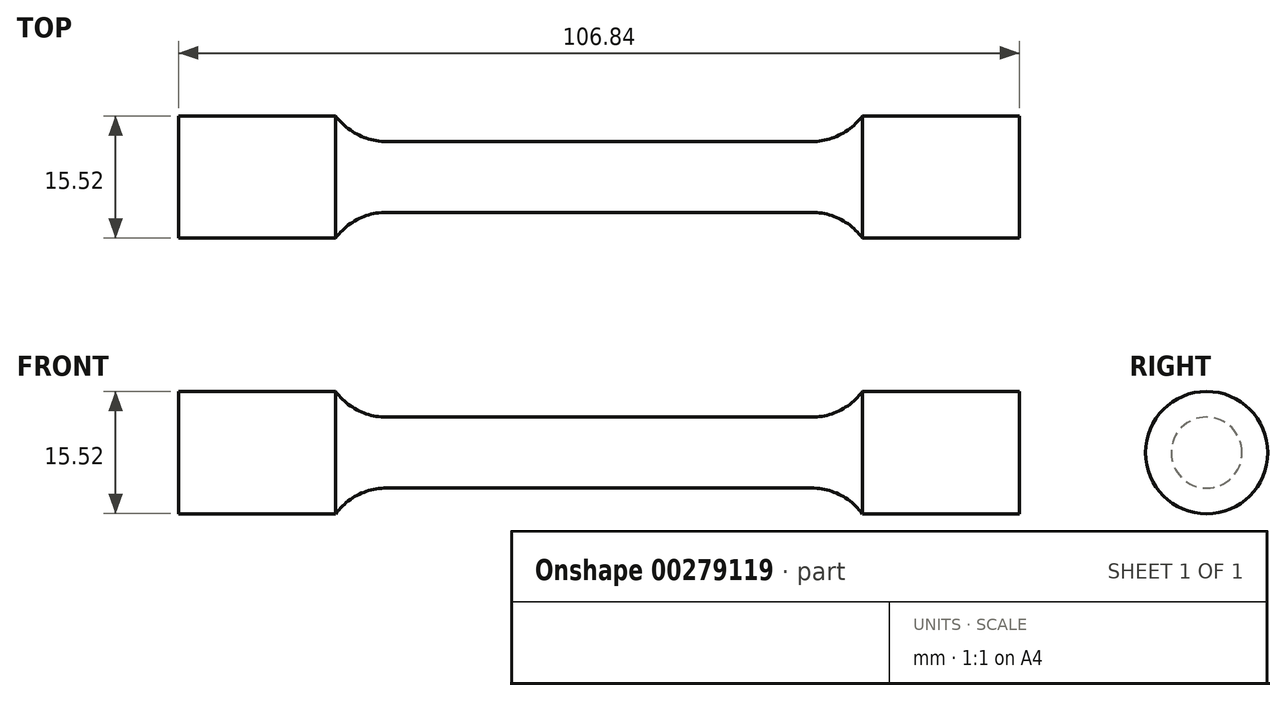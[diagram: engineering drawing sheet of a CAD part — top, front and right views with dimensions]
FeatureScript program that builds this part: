
annotation { "Feature Type Name" : "Feature", "Feature Type Description" : "" }
export const myFeature = defineFeature(function(context is Context, id is Id, definition is map)
    precondition{}
    {
        {
            var Q0;
            Q0=qCreatedBy(makeId("Front.planeOp"),FACE);
            var sketch = newSketch(context, id + "F0", { "sketchPlane" : qUnion([Q0])});
            skLineSegment(sketch, "E0", {"start": v(0, 4.5) * mm, "end": v(27, 4.5) * mm});
            skArc(sketch, "E1", {"start": v(27, 4.5) * mm, "mid": v(30.61, 5.36) * mm, "end": v(33.45, 7.76) * mm});
            skLineSegment(sketch, "E2", {"start": v(33.45, 7.76) * mm, "end": v(53.42, 7.76) * mm});
            skLineSegment(sketch, "E3", {"start": v(53.42, 7.76) * mm, "end": v(53.42, 0) * mm});
            skLineSegment(sketch, "E4", {"start": v(53.42, 0) * mm, "end": v(0, 0) * mm});
            skLineSegment(sketch, "E5.MirrorCS", {"start": v(0, 4.5) * mm, "end": v(-27, 4.5) * mm});
            skLineSegment(sketch, "E6.MirrorCS", {"start": v(-53.42, 0) * mm, "end": v(0, 0) * mm});
            skLineSegment(sketch, "E7.MirrorCS", {"start": v(-33.45, 7.76) * mm, "end": v(-53.42, 7.76) * mm});
            skLineSegment(sketch, "E8.MirrorCS", {"start": v(-53.42, 7.76) * mm, "end": v(-53.42, 0) * mm});
            skArc(sketch, "E9.MirrorCS", {"start": v(-27, 4.5) * mm, "mid": v(-30.61, 5.36) * mm, "end": v(-33.45, 7.76) * mm});
            skSolve(sketch);
        }
        {
            var Q0;
            Q0=makeQuery(id+"F0.imprint","IMPRINT",FACE,{"disambiguationData":[TD([[makeQuery(id+"F0.imprint","IMPRINT",EDGE,{"derivedFrom":sQuery(id+"F0.wireOp",EDGE,"E0")}),-1.0]])]});
            var Q1;
            Q1=sQuery(id+"F0.wireOp",EDGE,"E6.MirrorCS");
            revolve(context, id + "F1", {"entities" : qUnion([Q0]), "axis" : qUnion([Q1]), "revolveType" : RevolveType.FULL});
        }
    });
